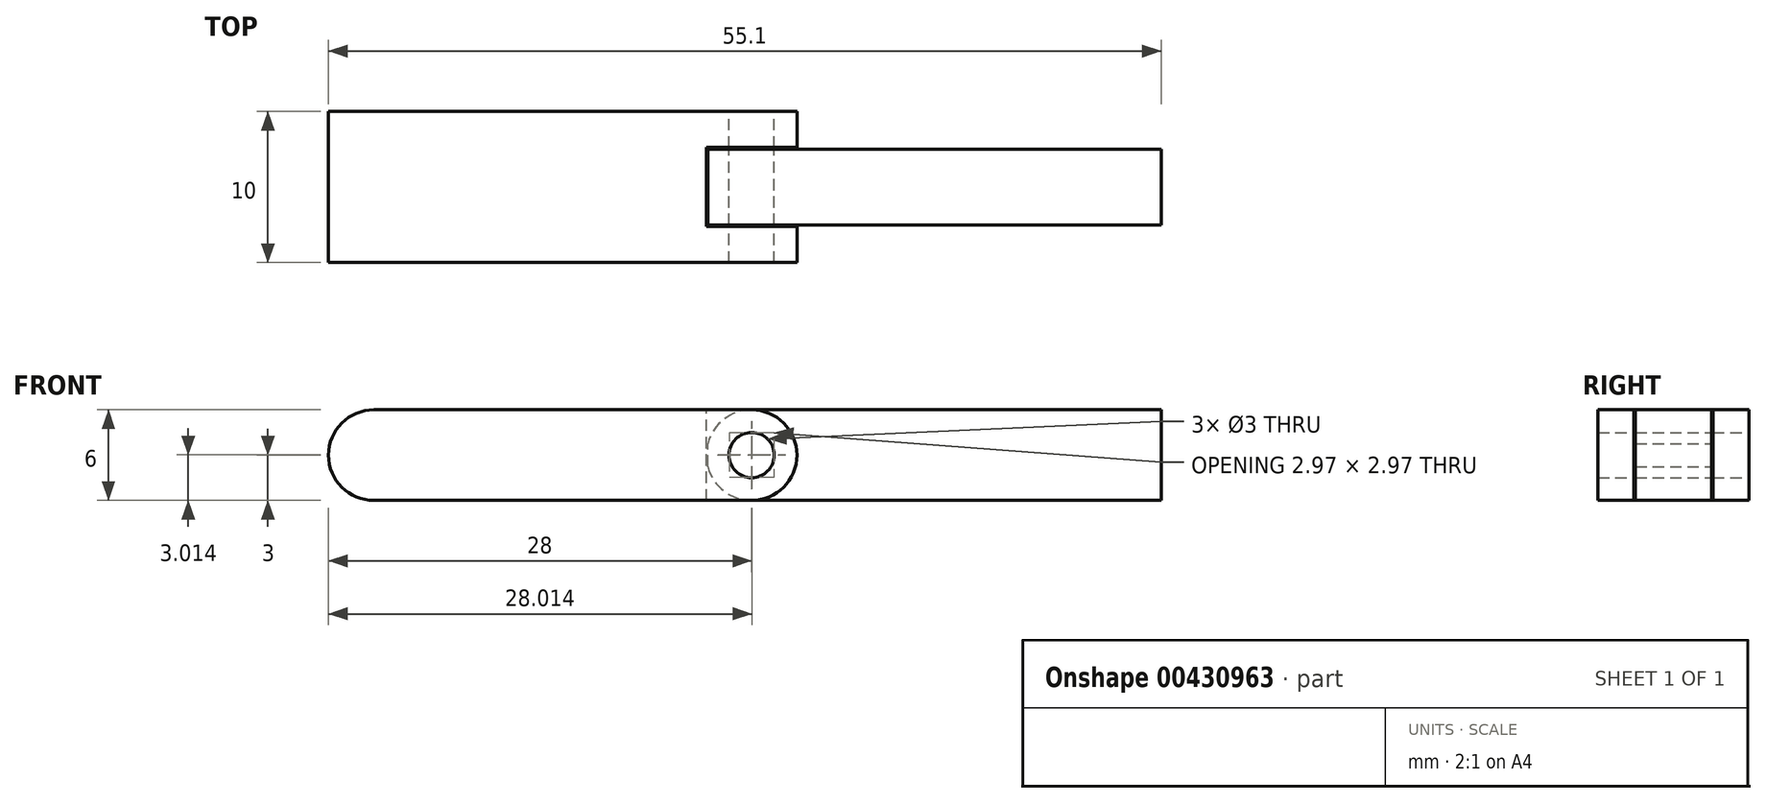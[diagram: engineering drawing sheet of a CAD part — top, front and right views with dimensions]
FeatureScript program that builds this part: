
annotation { "Feature Type Name" : "Feature", "Feature Type Description" : "" }
export const myFeature = defineFeature(function(context is Context, id is Id, definition is map)
    precondition{}
    {
        {
            var Q0;
            Q0=qCreatedBy(makeId("Front.planeOp"),FACE);
            var sketch = newSketch(context, id + "F0", { "sketchPlane" : qUnion([Q0])});
            skCircle(sketch, "E0", {"center": v(0, 0) * mm, "radius": 1.5 * mm});
            skLineSegment(sketch, "E1", {"start": v(0, 3) * mm, "end": v(-25, 3) * mm});
            skLineSegment(sketch, "E2", {"start": v(0, -3) * mm, "end": v(-25, -3) * mm});
            skArc(sketch, "E3", {"start": v(-25, 3) * mm, "mid": v(-28, 0) * mm, "end": v(-25, -3) * mm});
            skArc(sketch, "E4", {"start": v(0, 3) * mm, "mid": v(3, 0) * mm, "end": v(0, -3) * mm});
            skSolve(sketch);
        }
        {
            var Q0;
            Q0=makeQuery(id+"F0.imprint","IMPRINT",FACE,{"disambiguationData":[TD([[makeQuery(id+"F0.imprint","IMPRINT",EDGE,{"derivedFrom":sQuery(id+"F0.wireOp",EDGE,"E0")}),-1.0]])]});
            extrude(context, id + "F1", {"entities" : qUnion([Q0]), "depth" : 5 * mm, "hasSecondDirection" : true, "secondDirectionOppositeDirection" : true, "secondDirectionDepth" : 5 * mm});
        }
        {
            var Q0;
            Q0=makeQuery(id+"F1.opExtrude","SWEPT_FACE",FACE,{"disambiguationData":[OSD([sQuery(id+"F0.wireOp",EDGE,"E1")])]});
            var sketch = newSketch(context, id + "F2", { "sketchPlane" : qUnion([Q0])});
            skLineSegment(sketch, "E5", {"start": v(3, 5) * mm, "end": v(3, -5) * mm});
            skLineSegment(sketch, "E6.bottom", {"start": v(3, -2.61) * mm, "end": v(-3, -2.61) * mm});
            skLineSegment(sketch, "E6.top", {"start": v(3, 2.61) * mm, "end": v(0, 2.61) * mm});
            skLineSegment(sketch, "E6.left", {"start": v(3, -2.61) * mm, "end": v(3, 2.61) * mm});
            skLineSegment(sketch, "E6.right", {"start": v(-3, -2.61) * mm, "end": v(-3, 0) * mm});
            skLineSegment(sketch, "E7", {"start": v(-3, 0) * mm, "end": v(-3, 2.61) * mm});
            skPoint(sketch, "E8.0", {"position": v(0, 0) * mm});
            skLineSegment(sketch, "E9", {"start": v(4.2, 0) * mm, "end": v(-4.5, 0) * mm, "construction": true});
            skLineSegment(sketch, "E10", {"start": v(0, 2.61) * mm, "end": v(-3, 2.61) * mm});
            skSolve(sketch);
        }
        {
            var Q0;
            {var subQ0=sQuery(id+"F2.wireOp",EDGE,"E6.right");Q0=makeQuery(id+"F2.imprint","IMPRINT",FACE,{"disambiguationData":[TD([[makeQuery(id+"F2.imprint","IMPRINT",EDGE,{"derivedFrom":subQ0}),-1.0]])]});}
            var Q1;
            {var subQ4=sQuery(id+"F2.wireOp",EDGE,"E6.top");Q1=makeQuery(id+"F2.imprint","IMPRINT",FACE,{"disambiguationData":[TD([[makeQuery(id+"F2.imprint","IMPRINT",EDGE,{"derivedFrom":subQ4}),1.0]])]});}
            extrude(context, id + "F3", {"entities" : qUnion([Q0, Q1]), "operationType" : NewBodyOperationType.REMOVE, "oppositeDirection" : true, "depth" : 25 * mm});
        }
        {
            var Q0;
            Q0=makeQuery(id+"F1.opExtrude","SWEPT_FACE",FACE,{"disambiguationData":[OSD([sQuery(id+"F0.wireOp",EDGE,"E1")])]});
            var sketch = newSketch(context, id + "F4", { "sketchPlane" : qUnion([Q0])});
            skLineSegment(sketch, "E11.bottom", {"start": v(-2.9, -2.51) * mm, "end": v(27.1, -2.51) * mm});
            skLineSegment(sketch, "E11.top", {"start": v(-2.9, 2.51) * mm, "end": v(27.1, 2.51) * mm});
            skLineSegment(sketch, "E11.left", {"start": v(-2.9, -2.51) * mm, "end": v(-2.9, 2.51) * mm});
            skLineSegment(sketch, "E11.right", {"start": v(27.1, -2.51) * mm, "end": v(27.1, 2.51) * mm});
            skSolve(sketch);
        }
        {
            var Q0;
            Q0=makeQuery(id+"F4.imprint","IMPRINT",FACE,{"disambiguationData":[TD([[makeQuery(id+"F4.imprint","IMPRINT",EDGE,{"derivedFrom":sQuery(id+"F4.wireOp",EDGE,"E11.bottom")}),1.0]])]});
            var Q1;
            Q1=makeQuery(id+"F1.opExtrude","SWEPT_FACE",FACE,{"disambiguationData":[OSD([sQuery(id+"F0.wireOp",EDGE,"E2")])]});
            extrude(context, id + "F5", {"entities" : qUnion([Q0]), "endBound" : BoundingType.UP_TO_SURFACE, "oppositeDirection" : true, "endBoundEntityFace" : qUnion([Q1]), "depth" : 22 * mm});
        }
        {
            var Q0;
            Q0=makeQuery(id+"F5.opExtrude","SWEPT_FACE",FACE,{"disambiguationData":[OSD([sQuery(id+"F4.wireOp",EDGE,"E11.top")])]});
            var sketch = newSketch(context, id + "F6", { "sketchPlane" : qUnion([Q0])});
            skCircle(sketch, "E12.0", {"center": v(0, 0) * mm, "radius": 1.5 * mm});
            skPoint(sketch, "E13", {"position": v(0, -1.5) * mm});
            skLineSegment(sketch, "E14", {"start": v(0, 3) * mm, "end": v(2.9, 3) * mm});
            skLineSegment(sketch, "E15", {"start": v(2.9, 3) * mm, "end": v(2.9, 0.77) * mm});
            skLineSegment(sketch, "E16", {"start": v(0, -3) * mm, "end": v(2.9, -3) * mm});
            skLineSegment(sketch, "E17", {"start": v(2.9, -3) * mm, "end": v(2.9, -0.77) * mm});
            skLineSegment(sketch, "E18", {"start": v(2.9, 0.77) * mm, "end": v(2.9, 0.77) * mm});
            skLineSegment(sketch, "E19", {"start": v(2.9, -0.77) * mm, "end": v(2.9, -0.77) * mm});
            skArc(sketch, "E20", {"start": v(0, 3) * mm, "mid": v(1.83, 2.38) * mm, "end": v(2.9, 0.77) * mm});
            skArc(sketch, "E21", {"start": v(2.9, -0.77) * mm, "mid": v(1.83, -2.38) * mm, "end": v(0, -3) * mm});
            skSolve(sketch);
        }
        {
            var Q0;
            Q0=makeQuery(id+"F6.imprint","IMPRINT",FACE,{"disambiguationData":[TD([[makeQuery(id+"F6.imprint","IMPRINT",EDGE,{"derivedFrom":sQuery(id+"F6.wireOp",EDGE,"E12.0")}),1.0]])]});
            var Q1;
            Q1=makeQuery(id+"F6.imprint","IMPRINT",FACE,{"disambiguationData":[TD([[makeQuery(id+"F6.imprint","IMPRINT",EDGE,{"derivedFrom":sQuery(id+"F6.wireOp",EDGE,"E14")}),1.0]])]});
            var Q2;
            Q2=makeQuery(id+"F6.imprint","IMPRINT",FACE,{"disambiguationData":[TD([[makeQuery(id+"F6.imprint","IMPRINT",EDGE,{"derivedFrom":sQuery(id+"F6.wireOp",EDGE,"E16")}),-1.0]])]});
            var Q3;
            Q3=makeQuery(id+"F5.opExtrude","SWEPT_FACE",FACE,{"disambiguationData":[OSD([sQuery(id+"F4.wireOp",EDGE,"E11.bottom")])]});
            extrude(context, id + "F7", {"entities" : qUnion([Q0, Q1, Q2]), "operationType" : NewBodyOperationType.REMOVE, "endBound" : BoundingType.UP_TO_SURFACE, "oppositeDirection" : true, "endBoundEntityFace" : qUnion([Q3]), "depth" : 25 * mm});
        }
    });
